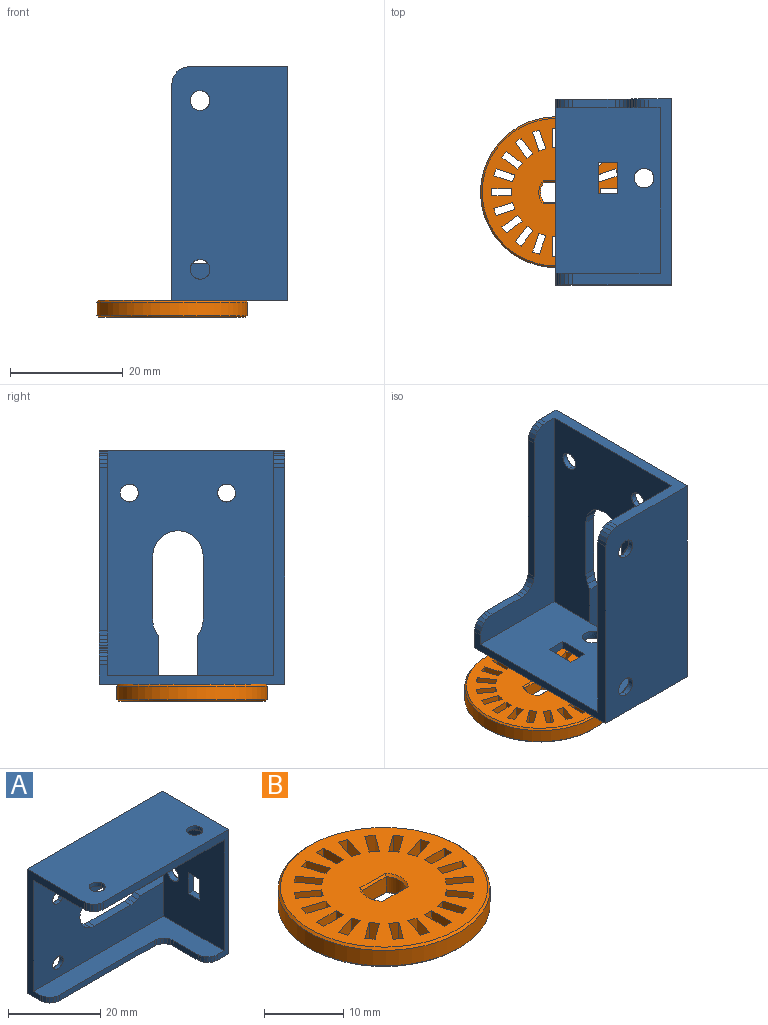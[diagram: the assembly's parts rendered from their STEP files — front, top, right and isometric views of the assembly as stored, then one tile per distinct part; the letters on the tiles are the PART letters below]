
ASSEMBLY  parts=2 mates=1
PART A: 101 faces, bbox 41.5x20.5x33 mm
  f0: extruded ~3.5x1.97mm, area 5.7mm2, adj f8,f14,f23
  f1: bspline ~3.48x2.69mm, area 8.5mm2, adj f9,f13,f79
  f2: extruded ~3.49x1.75mm, area 5.3mm2, adj f8,f12,f41
  f3: extruded ~3.19x1.8mm, area 5.2mm2, adj f11,f45,f80
  f4: plane 8.67x2mm, normal (0,0,-1), area 17.3mm2, adj f6,f9,f48,f62,f80
  f5: plane 8.67x2mm, normal (0,0,1), area 17.3mm2, adj f6,f9,f48,f67,f80
  f6: plane 41.5x33mm, normal (0,1,0), area 1095.8mm2, adj f4,f5,f7,f8,f9,f10,f42,f44
  f7: plane 2x0.93mm, normal (0.61,0,-0.79), area 2.3mm2, adj f6,f60,f63,f80
  f8: plane 41.51x20.51mm, normal (0,0,1), area 829.5mm2, adj f0,f2,f6,f9,f12,f23,f28,f29
  f9: plane 33.01x20.51mm, normal (1,0,0), area 633.7mm2, adj f1,f4,f5,f6,f8,f10,f13,f19
  f10: plane 41.5x20.5mm, normal (0,0,-1), area 376.2mm2, adj f6,f9,f27,f30,f31,f32,f33,f34
  f11: cylinder r=1.6mm len=3.19mm, axis (0,1,0), area 4.8mm2, adj f3,f45,f80
  f12: extruded ~3.5x1.97mm, area 5.7mm2, adj f2,f8,f41
  f13: bspline ~3.41x2.49mm, area 7.9mm2, adj f1,f9,f79
  f14: plane 6.59x5.71mm, normal (0,0,-1), area 18.5mm2, adj f0,f15,f17,f18,f23,f24,f25,f40
  f15: plane 3.29x1mm, normal (0,1,0), area 3.3mm2, adj f14,f17,f40,f50
  f16: plane 3.29x1mm, normal (0,-1,0), area 3.3mm2, adj f26,f38,f41,f50
  f17: plane 2.85x1.65mm, normal (0.87,0.5,0), area 3.3mm2, adj f14,f15,f25,f50
  f18: plane 2.85x1.65mm, normal (-0.87,-0.5,0), area 3.3mm2, adj f14,f24,f40,f50
  f19: plane 5.5x1.5mm, normal (0,-1,0), area 8.2mm2, adj f9,f22,f39,f79
  f20: plane 3.29x1mm, normal (0,1,0), area 3.3mm2, adj f21,f41,f43,f50
  f21: plane 2.85x1.65mm, normal (-0.87,0.5,0), area 3.3mm2, adj f20,f26,f41,f50
  f22: plane 3.5x1.5mm, normal (0,0,1), area 5.3mm2, adj f9,f19,f56,f79
  f23: extruded ~3.49x1.75mm, area 5.3mm2, adj f0,f8,f14
  f24: plane 3.29x1mm, normal (0,-1,0), area 3.3mm2, adj f14,f18,f25,f50
  f25: plane 2.85x1.65mm, normal (0.87,-0.5,0), area 3.3mm2, adj f14,f17,f24,f50
  f26: plane 2.85x1.65mm, normal (-0.87,-0.5,0), area 3.3mm2, adj f16,f21,f41,f50
  f27: plane 1.5x0.72mm, normal (-0.38,-0.92,0), area 1.2mm2, adj f10,f30,f31,f52
  f28: plane 2x0.78mm, normal (-0.13,-0.99,0), area 1.6mm2, adj f8,f34,f35,f50
  f29: plane 2x0.62mm, normal (-0.79,-0.61,0), area 1.6mm2, adj f8,f36,f37,f50
  f30: plane 1.5x0.78mm, normal (-0.13,-0.99,0), area 1.2mm2, adj f10,f27,f34,f52
  f31: plane 1.5x0.62mm, normal (-0.61,-0.79,0), area 1.2mm2, adj f10,f27,f32,f52
  f32: plane 1.5x0.62mm, normal (-0.79,-0.61,0), area 1.2mm2, adj f10,f31,f33,f52
  f33: plane 1.5x0.72mm, normal (-0.92,-0.38,0), area 1.2mm2, adj f10,f32,f52,f83
  f34: plane 38.5x33mm, normal (0,-1,0), area 126.5mm2, adj f8,f9,f10,f28,f30,f50,f52,f79
  f35: plane 2x0.72mm, normal (-0.38,-0.92,0), area 1.6mm2, adj f8,f28,f37,f50
  f36: plane 2x0.72mm, normal (-0.92,-0.38,0), area 1.6mm2, adj f8,f29,f50,f94
  f37: plane 2x0.62mm, normal (-0.61,-0.79,0), area 1.6mm2, adj f8,f29,f35,f50
  f38: plane 2.85x1.65mm, normal (0.87,-0.5,0), area 3.3mm2, adj f16,f41,f43,f50
  f39: plane 3.5x1.5mm, normal (0,0,-1), area 5.3mm2, adj f9,f19,f56,f79
  f40: plane 2.85x1.65mm, normal (-0.87,0.5,0), area 3.3mm2, adj f14,f15,f18,f50
  f41: plane 6.59x5.71mm, normal (0,0,-1), area 18.5mm2, adj f2,f12,f16,f20,f21,f26,f38,f43
  f42: plane 2.85x1.65mm, normal (-0.87,0,0.5), area 3.3mm2, adj f6,f44,f45,f77
  f43: plane 2.85x1.65mm, normal (0.87,0.5,0), area 3.3mm2, adj f20,f38,f41,f50
  f44: plane 2.85x1.65mm, normal (-0.87,0,-0.5), area 3.3mm2, adj f6,f42,f45,f99
  f45: plane 6.59x5.71mm, normal (0,1,0), area 20.1mm2, adj f3,f11,f42,f44,f46,f51,f77,f99
  f46: plane 2.85x1.65mm, normal (0.87,0,0.5), area 3.3mm2, adj f6,f45,f51,f77
  f47: plane 3.29x1mm, normal (0,0,1), area 3.3mm2, adj f6,f78,f81,f98
  f48: plane 7x1.5mm, normal (0,1,0), area 10.5mm2, adj f4,f5,f9,f79
  f49: plane 2.85x1.65mm, normal (-0.87,0,-0.5), area 3.3mm2, adj f6,f57,f78,f98
  f50: plane 40x18.5mm, normal (0,0,-1), area 681.7mm2, adj f15,f16,f17,f18,f20,f21,f24,f25
  f51: plane 2.85x1.65mm, normal (0.87,0,-0.5), area 3.3mm2, adj f6,f45,f46,f99
  f52: plane 40x18.5mm, normal (0,0,1), area 265.5mm2, adj f27,f30,f31,f32,f33,f34,f79,f80
  f53: bspline ~3.19x2.51mm, area 5.7mm2, adj f54,f78,f80
  f54: bspline ~2.96x1.9mm, area 4.4mm2, adj f53,f78,f80
  f55: plane 2.85x1.65mm, normal (0.87,0,-0.5), area 3.3mm2, adj f6,f57,f78,f81
  f56: plane 5.5x1.5mm, normal (0,1,0), area 8.2mm2, adj f9,f22,f39,f79
  f57: plane 3.29x1mm, normal (0,0,-1), area 3.3mm2, adj f6,f49,f55,f78
  f58: plane 11.19x2mm, normal (0,0,1), area 22.4mm2, adj f6,f61,f76,f80
  f59: plane 2x0.93mm, normal (0.79,0,0.61), area 2.3mm2, adj f6,f66,f75,f80
  f60: plane 2x1.09mm, normal (0.38,0,-0.92), area 2.3mm2, adj f6,f7,f71,f80
  f61: plane 2x1.05mm, normal (-0.09,0,1), area 2.1mm2, adj f6,f58,f64,f80
  f62: plane 2x0.89mm, normal (-0.53,0,-0.85), area 2.1mm2, adj f4,f6,f74,f80
  f63: plane 2x0.93mm, normal (0.79,0,-0.61), area 2.3mm2, adj f6,f7,f68,f80
  f64: plane 2x1mm, normal (-0.32,0,0.95), area 2.1mm2, adj f6,f61,f67,f80
  f65: plane 2x1.05mm, normal (-0.09,0,-1), area 2.1mm2, adj f6,f70,f74,f80
  f66: plane 2x1.09mm, normal (0.92,0,0.38), area 2.3mm2, adj f6,f59,f73,f80
  f67: plane 2x0.89mm, normal (-0.53,0,0.85), area 2.1mm2, adj f5,f6,f64,f80
  f68: plane 2x1.09mm, normal (0.92,0,-0.38), area 2.3mm2, adj f6,f63,f72,f80
  f69: plane 2x1.09mm, normal (0.38,0,0.92), area 2.3mm2, adj f6,f75,f76,f80
  f70: plane 11.19x2mm, normal (0,0,-1), area 22.4mm2, adj f6,f65,f71,f80
  f71: plane 2x1.16mm, normal (0.13,0,-0.99), area 2.3mm2, adj f6,f60,f70,f80
  f72: plane 2x1.16mm, normal (0.99,0,-0.13), area 2.3mm2, adj f6,f68,f73,f80
  f73: plane 2x1.16mm, normal (0.99,0,0.13), area 2.3mm2, adj f6,f66,f72,f80
  f74: plane 2x1mm, normal (-0.32,0,-0.95), area 2.1mm2, adj f6,f62,f65,f80
  f75: plane 2x0.93mm, normal (0.61,0,0.79), area 2.3mm2, adj f6,f59,f69,f80
  f76: plane 2x1.16mm, normal (0.13,0,0.99), area 2.3mm2, adj f6,f58,f69,f80
  f77: plane 3.29x1mm, normal (0,0,1), area 3.3mm2, adj f6,f42,f45,f46
  f78: plane 6.58x5.7mm, normal (0,1,0), area 20.1mm2, adj f47,f49,f53,f54,f55,f57,f81,f98
  f79: plane 29.52x18.52mm, normal (-1,0,0), area 516.9mm2, adj f1,f13,f19,f22,f34,f39,f48,f50
  f80: plane 40.01x29.51mm, normal (0,-1,0), area 957mm2, adj f3,f4,f5,f7,f11,f50,f52,f53
  f81: plane 2.85x1.65mm, normal (0.87,0,0.5), area 3.3mm2, adj f6,f47,f55,f78
  f82: plane 1.5x0.78mm, normal (-0.99,-0.13,0), area 1.2mm2, adj f10,f52,f93,f100
  f83: plane 1.5x0.78mm, normal (-0.99,-0.13,0), area 1.2mm2, adj f10,f33,f52,f97
  f84: plane 1.5x0.62mm, normal (-0.79,-0.61,0), area 1.2mm2, adj f10,f52,f89,f96
  f85: plane 1.5x0.78mm, normal (-0.13,-0.99,0), area 1.2mm2, adj f10,f52,f86,f87
  f86: plane 1.5x0.72mm, normal (-0.38,-0.92,0), area 1.2mm2, adj f10,f52,f85,f95
  f87: plane 29x1.5mm, normal (0,-1,0), area 43.5mm2, adj f10,f52,f85,f91
  f88: plane 1.5x0.72mm, normal (-0.38,-0.92,0), area 1.2mm2, adj f10,f52,f89,f91
  f89: plane 1.5x0.62mm, normal (-0.61,-0.79,0), area 1.2mm2, adj f10,f52,f84,f88
  f90: plane 1.5x0.78mm, normal (-0.99,-0.13,0), area 1.2mm2, adj f10,f52,f96,f97
  f91: plane 1.5x0.78mm, normal (-0.13,-0.99,0), area 1.2mm2, adj f10,f52,f87,f88
  f92: plane 1.5x0.62mm, normal (-0.79,-0.61,0), area 1.2mm2, adj f10,f52,f93,f95
  f93: plane 1.5x0.72mm, normal (-0.92,-0.38,0), area 1.2mm2, adj f10,f52,f82,f92
  f94: plane 2x0.78mm, normal (-0.99,-0.13,0), area 1.6mm2, adj f8,f36,f50,f100
  f95: plane 1.5x0.62mm, normal (-0.61,-0.79,0), area 1.2mm2, adj f10,f52,f86,f92
  f96: plane 1.5x0.72mm, normal (-0.92,-0.38,0), area 1.2mm2, adj f10,f52,f84,f90
  f97: plane 7.5x1.5mm, normal (-1,0,0), area 11.3mm2, adj f10,f52,f83,f90
  f98: plane 2.85x1.65mm, normal (-0.87,0,0.5), area 3.3mm2, adj f6,f47,f49,f78
  f99: plane 3.29x1mm, normal (0,0,-1), area 3.3mm2, adj f6,f44,f45,f51
  f100: plane 33x17.5mm, normal (-1,0,0), area 100mm2, adj f6,f8,f10,f50,f52,f80,f82,f94
PART B: 97 faces, bbox 26.8x26.8x3 mm
  f0: plane 26.2x26.2mm, normal (0,0,-1), area 425.2mm2, adj f1,f2,f3,f4,f5,f6,f7,f8
  f1: cone r=13.4mm half-angle=45deg, axis (0,0,1), area 35.3mm2, adj f0,f86
  f2: plane 4.52x0.31mm, normal (0,-0.71,-0.71), area 1.9mm2, adj f0,f3,f4,f87
  f3: cone r=2.75mm half-angle=45deg, axis (0,0,-1), area 1.8mm2, adj f0,f2,f5,f88
  f4: cone r=2.75mm half-angle=45deg, axis (0,0,-1), area 1.8mm2, adj f0,f2,f5,f89
  f5: plane 4.52x0.31mm, normal (0,0.71,-0.71), area 1.9mm2, adj f0,f3,f4,f90
  f6: plane 3x1.05mm, normal (0.81,0.59,0), area 3.9mm2, adj f0,f7,f9,f91
  f7: plane 3x2.83mm, normal (0.59,-0.81,0), area 10.5mm2, adj f0,f6,f8,f91
  f8: plane 3x1.05mm, normal (-0.81,-0.59,0), area 3.9mm2, adj f0,f7,f9,f91
  f9: plane 3x2.83mm, normal (-0.59,0.81,0), area 10.5mm2, adj f0,f6,f8,f91
  f10: plane 3.33x3mm, normal (-0.31,0.95,0), area 10.5mm2, adj f0,f11,f13,f91
  f11: plane 3x1.24mm, normal (0.95,0.31,0), area 3.9mm2, adj f0,f10,f12,f91
  f12: plane 3.33x3mm, normal (0.31,-0.95,0), area 10.5mm2, adj f0,f11,f13,f91
  f13: plane 3x1.24mm, normal (-0.95,-0.31,0), area 3.9mm2, adj f0,f10,f12,f91
  f14: plane 3x1.24mm, normal (0.31,0.95,0), area 3.9mm2, adj f0,f15,f17,f91
  f15: plane 3.33x3mm, normal (0.95,-0.31,0), area 10.5mm2, adj f0,f14,f16,f91
  f16: plane 3x1.24mm, normal (-0.31,-0.95,0), area 3.9mm2, adj f0,f15,f17,f91
  f17: plane 3.33x3mm, normal (-0.95,0.31,0), area 10.5mm2, adj f0,f14,f16,f91
  f18: plane 3x1.05mm, normal (0.59,0.81,0), area 3.9mm2, adj f0,f19,f21,f91
  f19: plane 3x2.83mm, normal (0.81,-0.59,0), area 10.5mm2, adj f0,f18,f20,f91
  f20: plane 3x1.05mm, normal (-0.59,-0.81,0), area 3.9mm2, adj f0,f19,f21,f91
  f21: plane 3x2.83mm, normal (-0.81,0.59,0), area 10.5mm2, adj f0,f18,f20,f91
  f22: plane 3.5x3mm, normal (-1,0,0), area 10.5mm2, adj f0,f23,f25,f91
  f23: plane 3x1.3mm, normal (0,1,0), area 3.9mm2, adj f0,f22,f24,f91
  f24: plane 3.5x3mm, normal (1,0,0), area 10.5mm2, adj f0,f23,f25,f91
  f25: plane 3x1.3mm, normal (0,-1,0), area 3.9mm2, adj f0,f22,f24,f91
  f26: plane 3x2.83mm, normal (0.59,0.81,0), area 10.5mm2, adj f0,f27,f29,f91
  f27: plane 3x1.05mm, normal (0.81,-0.59,0), area 3.9mm2, adj f0,f26,f28,f91
  f28: plane 3x2.83mm, normal (-0.59,-0.81,0), area 10.5mm2, adj f0,f27,f29,f91
  f29: plane 3x1.05mm, normal (-0.81,0.59,0), area 3.9mm2, adj f0,f26,f28,f91
  f30: plane 3.33x3mm, normal (-0.31,-0.95,0), area 10.5mm2, adj f0,f31,f33,f91
  f31: plane 3x1.24mm, normal (-0.95,0.31,0), area 3.9mm2, adj f0,f30,f32,f91
  f32: plane 3.33x3mm, normal (0.31,0.95,0), area 10.5mm2, adj f0,f31,f33,f91
  f33: plane 3x1.24mm, normal (0.95,-0.31,0), area 3.9mm2, adj f0,f30,f32,f91
  f34: plane 3x1.05mm, normal (-0.59,0.81,0), area 3.9mm2, adj f0,f35,f37,f91
  f35: plane 3x2.83mm, normal (0.81,0.59,0), area 10.5mm2, adj f0,f34,f36,f91
  f36: plane 3x1.05mm, normal (0.59,-0.81,0), area 3.9mm2, adj f0,f35,f37,f91
  f37: plane 3x2.83mm, normal (-0.81,-0.59,0), area 10.5mm2, adj f0,f34,f36,f91
  f38: plane 3.33x3mm, normal (0.95,0.31,0), area 10.5mm2, adj f0,f39,f41,f91
  f39: plane 3x1.24mm, normal (0.31,-0.95,0), area 3.9mm2, adj f0,f38,f40,f91
  f40: plane 3.33x3mm, normal (-0.95,-0.31,0), area 10.5mm2, adj f0,f39,f41,f91
  f41: plane 3x1.24mm, normal (-0.31,0.95,0), area 3.9mm2, adj f0,f38,f40,f91
  f42: plane 3x1.3mm, normal (-1,0,0), area 3.9mm2, adj f0,f43,f45,f91
  f43: plane 3.5x3mm, normal (0,1,0), area 10.5mm2, adj f0,f42,f44,f91
  f44: plane 3x1.3mm, normal (1,0,0), area 3.9mm2, adj f0,f43,f45,f91
  f45: plane 3.5x3mm, normal (0,-1,0), area 10.5mm2, adj f0,f42,f44,f91
  f46: plane 3.5x3mm, normal (0,-1,0), area 10.5mm2, adj f0,f47,f49,f91
  f47: plane 3x1.3mm, normal (-1,0,0), area 3.9mm2, adj f0,f46,f48,f91
  f48: plane 3.5x3mm, normal (0,1,0), area 10.5mm2, adj f0,f47,f49,f91
  f49: plane 3x1.3mm, normal (1,0,0), area 3.9mm2, adj f0,f46,f48,f91
  f50: plane 3x2.83mm, normal (-0.59,-0.81,0), area 10.5mm2, adj f0,f51,f53,f91
  f51: plane 3x1.05mm, normal (-0.81,0.59,0), area 3.9mm2, adj f0,f50,f52,f91
  f52: plane 3x2.83mm, normal (0.59,0.81,0), area 10.5mm2, adj f0,f51,f53,f91
  f53: plane 3x1.05mm, normal (0.81,-0.59,0), area 3.9mm2, adj f0,f50,f52,f91
  f54: plane 3.33x3mm, normal (0.31,0.95,0), area 10.5mm2, adj f0,f55,f57,f91
  f55: plane 3x1.24mm, normal (0.95,-0.31,0), area 3.9mm2, adj f0,f54,f56,f91
  f56: plane 3.33x3mm, normal (-0.31,-0.95,0), area 10.5mm2, adj f0,f55,f57,f91
  f57: plane 3x1.24mm, normal (-0.95,0.31,0), area 3.9mm2, adj f0,f54,f56,f91
  f58: plane 3x1.05mm, normal (-0.59,0.81,0), area 3.9mm2, adj f0,f59,f61,f91
  f59: plane 3x2.83mm, normal (0.81,0.59,0), area 10.5mm2, adj f0,f58,f60,f91
  f60: plane 3x1.05mm, normal (0.59,-0.81,0), area 3.9mm2, adj f0,f59,f61,f91
  f61: plane 3x2.83mm, normal (-0.81,-0.59,0), area 10.5mm2, adj f0,f58,f60,f91
  f62: plane 3.33x3mm, normal (0.95,0.31,0), area 10.5mm2, adj f0,f63,f65,f91
  f63: plane 3x1.24mm, normal (0.31,-0.95,0), area 3.9mm2, adj f0,f62,f64,f91
  f64: plane 3.33x3mm, normal (-0.95,-0.31,0), area 10.5mm2, adj f0,f63,f65,f91
  f65: plane 3x1.24mm, normal (-0.31,0.95,0), area 3.9mm2, adj f0,f62,f64,f91
  f66: plane 3.33x3mm, normal (0.31,-0.95,0), area 10.5mm2, adj f0,f67,f69,f91
  f67: plane 3x1.24mm, normal (-0.95,-0.31,0), area 3.9mm2, adj f0,f66,f68,f91
  f68: plane 3.33x3mm, normal (-0.31,0.95,0), area 10.5mm2, adj f0,f67,f69,f91
  f69: plane 3x1.24mm, normal (0.95,0.31,0), area 3.9mm2, adj f0,f66,f68,f91
  f70: plane 3x1.05mm, normal (-0.81,-0.59,0), area 3.9mm2, adj f0,f71,f73,f91
  f71: plane 3x2.83mm, normal (-0.59,0.81,0), area 10.5mm2, adj f0,f70,f72,f91
  f72: plane 3x1.05mm, normal (0.81,0.59,0), area 3.9mm2, adj f0,f71,f73,f91
  f73: plane 3x2.83mm, normal (0.59,-0.81,0), area 10.5mm2, adj f0,f70,f72,f91
  f74: plane 3x2.83mm, normal (-0.81,0.59,0), area 10.5mm2, adj f0,f75,f77,f91
  f75: plane 3x1.05mm, normal (0.59,0.81,0), area 3.9mm2, adj f0,f74,f76,f91
  f76: plane 3x2.83mm, normal (0.81,-0.59,0), area 10.5mm2, adj f0,f75,f77,f91
  f77: plane 3x1.05mm, normal (-0.59,-0.81,0), area 3.9mm2, adj f0,f74,f76,f91
  f78: plane 3.33x3mm, normal (-0.95,0.31,0), area 10.5mm2, adj f0,f79,f81,f91
  f79: plane 3x1.24mm, normal (0.31,0.95,0), area 3.9mm2, adj f0,f78,f80,f91
  f80: plane 3.33x3mm, normal (0.95,-0.31,0), area 10.5mm2, adj f0,f79,f81,f91
  f81: plane 3x1.24mm, normal (-0.31,-0.95,0), area 3.9mm2, adj f0,f78,f80,f91
  f82: plane 3.5x3mm, normal (-1,0,0), area 10.5mm2, adj f0,f83,f84,f91
  f83: plane 3x1.3mm, normal (0,1,0), area 3.9mm2, adj f0,f82,f85,f91
  f84: plane 3x1.3mm, normal (0,-1,0), area 3.9mm2, adj f0,f82,f85,f91
  f85: plane 3.5x3mm, normal (1,0,0), area 10.5mm2, adj f0,f83,f84,f91
  f86: cylinder r=13.4mm len=26.8mm, axis (0,0,-1), area 202.1mm2, adj f1,f92
  f87: plane 4.24x2.4mm, normal (0,-1,0), area 10.2mm2, adj f2,f88,f89,f93
  f88: cylinder r=2.75mm len=3.5mm, axis (0,0,1), area 9.1mm2, adj f3,f87,f90,f94
  f89: cylinder r=2.75mm len=3.5mm, axis (0,0,1), area 9.1mm2, adj f4,f87,f90,f95
  f90: plane 4.24x2.4mm, normal (0,1,0), area 10.2mm2, adj f5,f88,f89,f96
  f91: plane 26.2x26.2mm, normal (0,0,1), area 425.2mm2, adj f6,f7,f8,f9,f10,f11,f12,f13
  f92: cone r=13.4mm half-angle=45deg, axis (0,0,-1), area 35.3mm2, adj f86,f91
  f93: plane 4.52x0.31mm, normal (0,-0.71,0.71), area 1.9mm2, adj f87,f91,f94,f95
  f94: cone r=2.75mm half-angle=45deg, axis (0,0,1), area 1.8mm2, adj f88,f91,f93,f96
  f95: cone r=2.75mm half-angle=45deg, axis (0,0,1), area 1.8mm2, adj f89,f91,f93,f96
  f96: plane 4.52x0.31mm, normal (0,0.71,0.71), area 1.9mm2, adj f90,f91,f94,f95
PLACE A rot(axis=(0.58,0.58,-0.58),120deg) t=(-80.91,-11.68,-21.13)mm
PLACE B t=(-63.19,-26.68,25.14)mm
MATE revolute A.f9 <-> B.f1  axis (0,0,-1) through (-63.19,-26.68,28.14)mm
